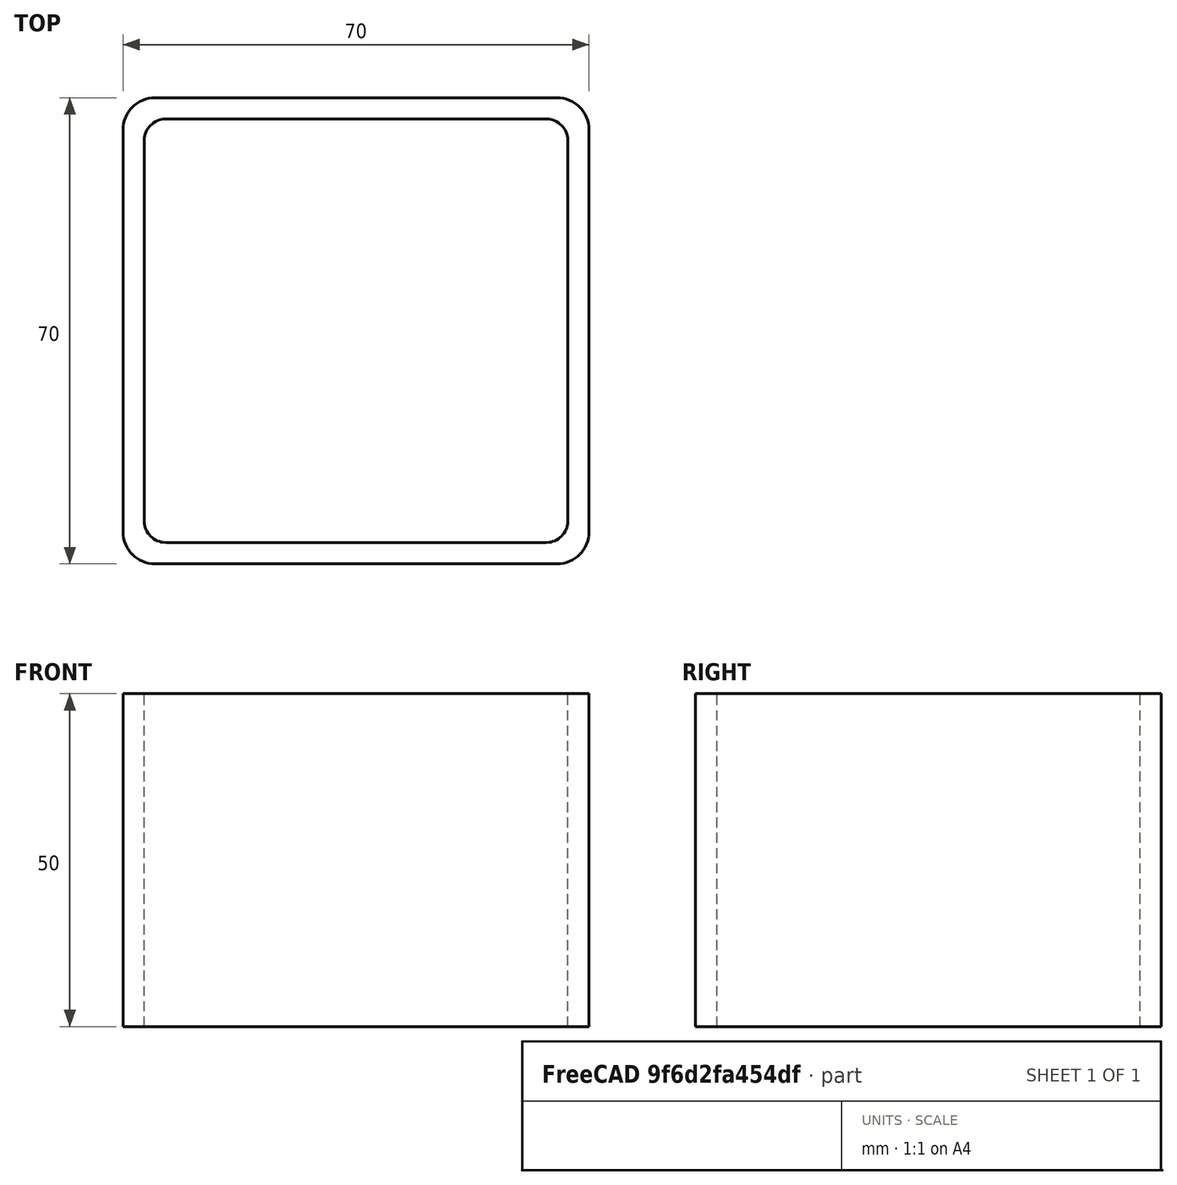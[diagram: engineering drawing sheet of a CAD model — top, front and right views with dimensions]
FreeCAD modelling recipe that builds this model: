
FCSTD DOCUMENT  (FreeCAD 0.15R4671 (Git))
Label: Square hollow section 70x70x3.2 EN10219 S235JRH
License: All rights reserved
LicenseURL: http://en.wikipedia.org/wiki/All_rights_reserved
objects: Sketcher::SketchObject×1, Part::Extrusion×1
note: 2 computed .brp shape members not serialized (recipe doc carries the construction recipe); baked Part::Feature solids carry a one-line shape summary decoded from their .brp

FEATURE [Sketcher::SketchObject] Sketch
  sketch-geometry (16):
    g0: LineSegment StartX=-28.6 StartY=31.8 StartZ=0 EndX=28.6 EndY=31.8 EndZ=0
    g1: LineSegment StartX=31.8 StartY=28.6 StartZ=0 EndX=31.8 EndY=-28.6 EndZ=0
    g2: LineSegment StartX=28.6 StartY=-31.8 StartZ=0 EndX=-28.6 EndY=-31.8 EndZ=0
    g3: LineSegment StartX=-31.8 StartY=-28.6 StartZ=0 EndX=-31.8 EndY=28.6 EndZ=0
    g4: LineSegment StartX=-30.2 StartY=35 StartZ=0 EndX=30.2 EndY=35 EndZ=0
    g5: LineSegment StartX=35 StartY=30.2 StartZ=0 EndX=35 EndY=-30.2 EndZ=0
    g6: LineSegment StartX=30.2 StartY=-35 StartZ=0 EndX=-30.2 EndY=-35 EndZ=0
    g7: LineSegment StartX=-35 StartY=-30.2 StartZ=0 EndX=-35 EndY=30.2 EndZ=0
    g8: ArcOfCircle CenterX=-28.6 CenterY=28.6 CenterZ=0 NormalX=0 NormalY=0 NormalZ=1 Radius=3.2 StartAngle=1.5708 EndAngle=3.14159
    g9: ArcOfCircle CenterX=28.6 CenterY=28.6 CenterZ=0 NormalX=0 NormalY=0 NormalZ=1 Radius=3.2 StartAngle=0 EndAngle=1.5708
    g10: ArcOfCircle CenterX=28.6 CenterY=-28.6 CenterZ=0 NormalX=0 NormalY=0 NormalZ=1 Radius=3.2 StartAngle=4.71239 EndAngle=6.28319
    g11: ArcOfCircle CenterX=-28.6 CenterY=-28.6 CenterZ=0 NormalX=0 NormalY=0 NormalZ=1 Radius=3.2 StartAngle=3.14159 EndAngle=4.71239
    g12: ArcOfCircle CenterX=30.2 CenterY=30.2 CenterZ=0 NormalX=0 NormalY=0 NormalZ=1 Radius=4.8 StartAngle=0 EndAngle=1.5708
    g13: ArcOfCircle CenterX=30.2 CenterY=-30.2 CenterZ=0 NormalX=0 NormalY=0 NormalZ=1 Radius=4.8 StartAngle=4.71239 EndAngle=6.28319
    g14: ArcOfCircle CenterX=-30.2 CenterY=-30.2 CenterZ=0 NormalX=0 NormalY=0 NormalZ=1 Radius=4.8 StartAngle=3.14159 EndAngle=4.71239
    g15: ArcOfCircle CenterX=-30.2 CenterY=30.2 CenterZ=0 NormalX=0 NormalY=0 NormalZ=1 Radius=4.8 StartAngle=1.5708 EndAngle=3.14159
  constraints (36):
    c: Horizontal(g2)
    c: Vertical(g3)
    c: Horizontal(g6)
    c: Vertical(g7)
    c: Tangent(g3,g8) = 1.5708
    c: Tangent(g0,g8) = 1.5708
    c: Tangent(g0,g9) = 1.5708
    c: Tangent(g1,g9) = 1.5708
    c: Tangent(g1,g10) = 1.5708
    c: Tangent(g2,g10) = 1.5708
    c: Tangent(g2,g11) = 1.5708
    c: Tangent(g3,g11) = 1.5708
    c: Tangent(g4,g12) = 1.5708
    c: Tangent(g5,g12) = 1.5708
    c: Tangent(g5,g13) = 1.5708
    c: Tangent(g6,g13) = 1.5708
    c: Tangent(g6,g14) = 1.5708
    c: Tangent(g7,g14) = 1.5708
    c: Tangent(g7,g15) = 1.5708
    c: Tangent(g4,g15) = 1.5708
    c: Equal(g9,g8)
    c: Equal(g9,g11)
    c: Equal(g9,g10)
    c: Equal(g12,g15)
    c: Equal(g12,g14)
    c: Equal(g12,g13)
    c: Symmetric(g4,g6,g-1)
    c: Symmetric(g7,g5,g-2)
    c: DistanceY(g4,g6) = -70
    c: DistanceX(g7,g5) = 70
    c: Symmetric(g3,g1,g-2)
    c: Symmetric(g0,g2,g-1)
    c: DistanceY(g0,g4) = 3.2
    c: DistanceX(g5,g1) = -3.2
    c: Radius(g9) = 3.2
    c: Radius(g12) = 4.8
FEATURE [Part::Extrusion] Extrude  label="Square hollow section 70x70x3.2 EN10219 S235JRH"
  Base = -> Sketch
  Dir = (0,0,50)
  Solid = true
